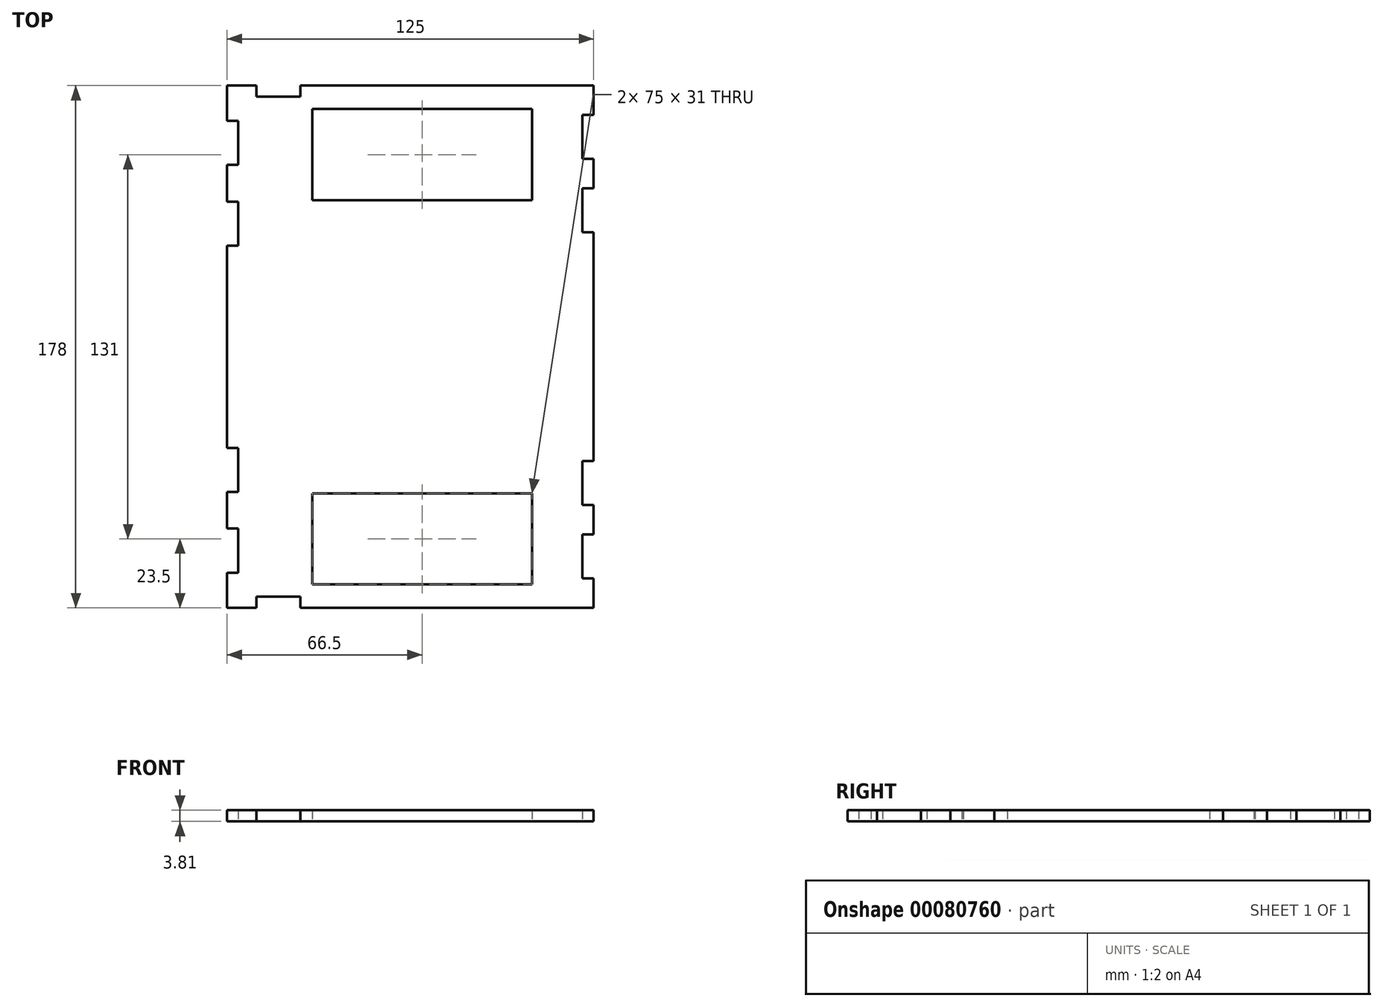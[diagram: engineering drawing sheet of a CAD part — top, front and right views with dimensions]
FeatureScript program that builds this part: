
annotation { "Feature Type Name" : "Feature", "Feature Type Description" : "" }
export const myFeature = defineFeature(function(context is Context, id is Id, definition is map)
    precondition{}
    {
        {
            var Q0;
            Q0=qCreatedBy(makeId("Top.planeOp"),FACE);
            var sketch = newSketch(context, id + "F0", { "sketchPlane" : qUnion([Q0])});
            skLineSegment(sketch, "E0.bottom", {"start": v(62.5, 89) * mm, "end": v(-62.5, 89) * mm});
            skLineSegment(sketch, "E0.top", {"start": v(62.5, -89) * mm, "end": v(-62.5, -89) * mm});
            skLineSegment(sketch, "E0.left", {"start": v(62.5, 89) * mm, "end": v(62.5, -89) * mm});
            skLineSegment(sketch, "E0.right", {"start": v(-62.5, 89) * mm, "end": v(-62.5, -89) * mm});
            skPoint(sketch, "E0.middle", {"position": v(0, 0) * mm});
            skLineSegment(sketch, "E1.bottom", {"start": v(41.5, 81) * mm, "end": v(-33.5, 81) * mm});
            skLineSegment(sketch, "E1.top", {"start": v(41.5, 50) * mm, "end": v(-33.5, 50) * mm});
            skLineSegment(sketch, "E1.left", {"start": v(41.5, 81) * mm, "end": v(41.5, 50) * mm});
            skLineSegment(sketch, "E1.right", {"start": v(-33.5, 81) * mm, "end": v(-33.5, 50) * mm});
            skPoint(sketch, "E1.middle", {"position": v(4, 65.5) * mm});
            skLineSegment(sketch, "E2", {"start": v(-62.5, 0) * mm, "end": v(62.5, 0) * mm, "construction": true});
            skLineSegment(sketch, "E3.MirrorCS", {"start": v(-33.5, -81) * mm, "end": v(-33.5, -50) * mm});
            skLineSegment(sketch, "E4.MirrorCS", {"start": v(41.5, -81) * mm, "end": v(-33.5, -81) * mm});
            skLineSegment(sketch, "E5.MirrorCS", {"start": v(41.5, -81) * mm, "end": v(41.5, -50) * mm});
            skLineSegment(sketch, "E6.MirrorCS", {"start": v(41.5, -50) * mm, "end": v(-33.5, -50) * mm});
            skLineSegment(sketch, "E7", {"start": v(-62.5, 22.5) * mm, "end": v(-38.5, 22.5) * mm});
            skLineSegment(sketch, "E8", {"start": v(-38.5, 22.5) * mm, "end": v(-38.5, 0) * mm});
            skLineSegment(sketch, "E9.MirrorCS", {"start": v(-38.5, -22.5) * mm, "end": v(-38.5, 0) * mm});
            skLineSegment(sketch, "E10.MirrorCS", {"start": v(-62.5, -22.5) * mm, "end": v(-38.5, -22.5) * mm});
            skLineSegment(sketch, "E11", {"start": v(-52.5, -89) * mm, "end": v(-52.5, -85.19) * mm});
            skLineSegment(sketch, "E12", {"start": v(-52.5, -85.19) * mm, "end": v(-37.5, -85.19) * mm});
            skLineSegment(sketch, "E13", {"start": v(-37.5, -85.19) * mm, "end": v(-37.5, -89) * mm});
            skLineSegment(sketch, "E14.MirrorCS", {"start": v(-52.5, 85.19) * mm, "end": v(-37.5, 85.19) * mm});
            skLineSegment(sketch, "E15.MirrorCS", {"start": v(-52.5, 89) * mm, "end": v(-52.5, 85.19) * mm});
            skLineSegment(sketch, "E16.MirrorCS", {"start": v(-37.5, 85.19) * mm, "end": v(-37.5, 89) * mm});
            skLineSegment(sketch, "E17", {"start": v(62.5, 79) * mm, "end": v(58.69, 79) * mm});
            skLineSegment(sketch, "E18", {"start": v(58.69, 79) * mm, "end": v(58.69, 64) * mm});
            skLineSegment(sketch, "E19", {"start": v(58.69, 64) * mm, "end": v(62.5, 64) * mm});
            skLineSegment(sketch, "E20", {"start": v(62.5, 54) * mm, "end": v(58.69, 54) * mm});
            skLineSegment(sketch, "E21", {"start": v(58.69, 54) * mm, "end": v(58.69, 39) * mm});
            skLineSegment(sketch, "E22", {"start": v(58.7, 39) * mm, "end": v(62.5, 39) * mm});
            skLineSegment(sketch, "E23.MirrorCS", {"start": v(58.7, -39) * mm, "end": v(62.5, -39) * mm});
            skLineSegment(sketch, "E24.MirrorCS", {"start": v(58.7, -54) * mm, "end": v(58.7, -39) * mm});
            skLineSegment(sketch, "E25.MirrorCS", {"start": v(62.5, -54) * mm, "end": v(58.69, -54) * mm});
            skLineSegment(sketch, "E26.MirrorCS", {"start": v(58.69, -64) * mm, "end": v(62.5, -64) * mm});
            skLineSegment(sketch, "E27.MirrorCS", {"start": v(58.7, -79) * mm, "end": v(58.7, -64) * mm});
            skLineSegment(sketch, "E28.MirrorCS", {"start": v(62.5, -79) * mm, "end": v(58.69, -79) * mm});
            skLineSegment(sketch, "E29", {"start": v(-62.5, 77) * mm, "end": v(-58.7, 77) * mm});
            skLineSegment(sketch, "E30", {"start": v(-58.7, 77) * mm, "end": v(-58.7, 62) * mm});
            skLineSegment(sketch, "E31", {"start": v(-58.7, 62) * mm, "end": v(-62.5, 62) * mm});
            skLineSegment(sketch, "E32", {"start": v(-62.5, 49.5) * mm, "end": v(-58.69, 49.5) * mm});
            skLineSegment(sketch, "E33", {"start": v(-58.7, 49.5) * mm, "end": v(-58.7, 34.5) * mm});
            skLineSegment(sketch, "E34", {"start": v(-58.7, 34.5) * mm, "end": v(-62.5, 34.5) * mm});
            skLineSegment(sketch, "E35.MirrorCS", {"start": v(-58.69, -49.5) * mm, "end": v(-58.69, -34.5) * mm});
            skLineSegment(sketch, "E36.MirrorCS", {"start": v(-58.7, -34.5) * mm, "end": v(-62.5, -34.5) * mm});
            skLineSegment(sketch, "E37.MirrorCS", {"start": v(-62.5, -49.5) * mm, "end": v(-58.69, -49.5) * mm});
            skLineSegment(sketch, "E38.MirrorCS", {"start": v(-58.7, -62) * mm, "end": v(-62.5, -62) * mm});
            skLineSegment(sketch, "E39.MirrorCS", {"start": v(-58.7, -77) * mm, "end": v(-58.7, -62) * mm});
            skLineSegment(sketch, "E40.MirrorCS", {"start": v(-62.5, -77) * mm, "end": v(-58.7, -77) * mm});
            skSolve(sketch);
        }
        {
            var Q0;
            Q0=makeQuery(id+"F0.imprint","IMPRINT",FACE,{"disambiguationData":[TD([[makeQuery(id+"F0.imprint","IMPRINT",EDGE,{"derivedFrom":sQuery(id+"F0.wireOp",EDGE,"E0.bottom")}),1.0]])]});
            var Q1;
            {var subQ0=sQuery(id+"F0.wireOp",EDGE,"E7");Q1=makeQuery(id+"F0.imprint","IMPRINT",FACE,{"disambiguationData":[TD([[makeQuery(id+"F0.imprint","IMPRINT",EDGE,{"derivedFrom":subQ0}),-1.0]])]});}
            extrude(context, id + "F1", {"entities" : qUnion([Q0, Q1]), "depth" : 3.8 * mm});
        }
    });
